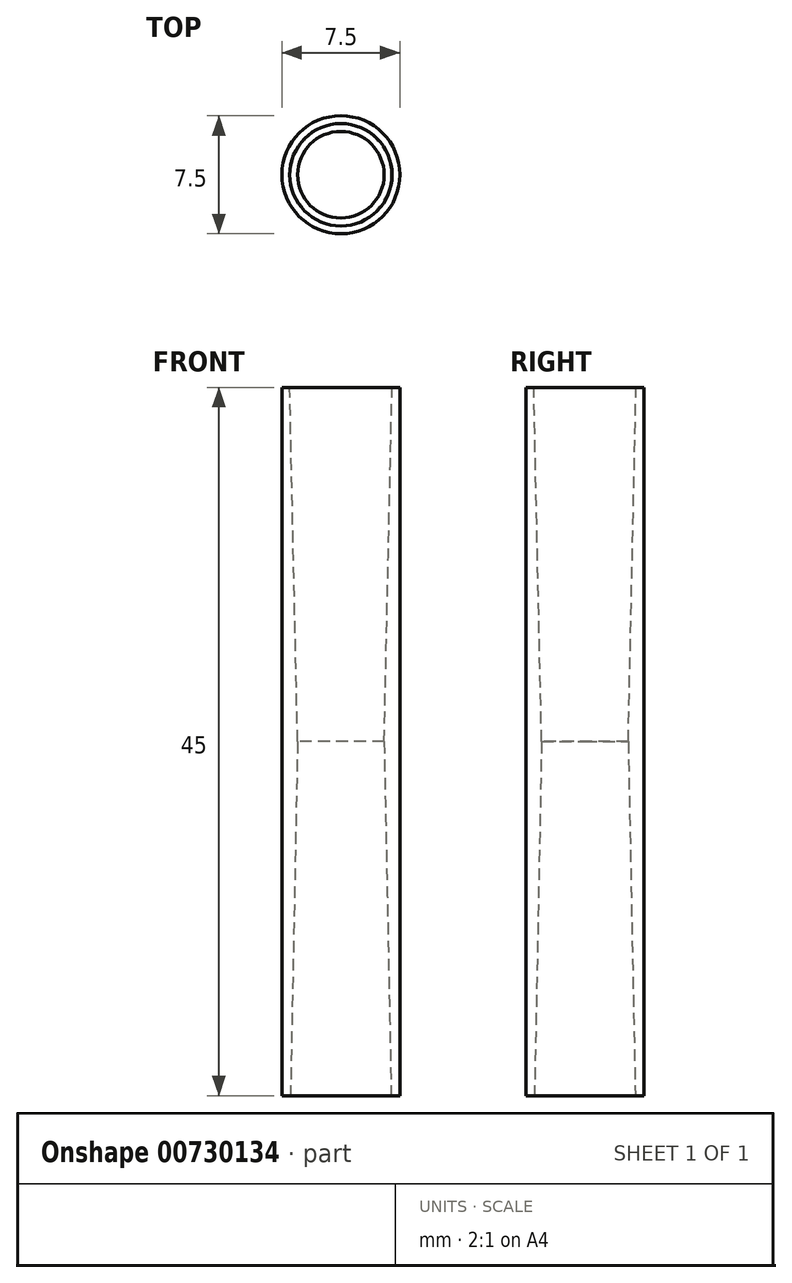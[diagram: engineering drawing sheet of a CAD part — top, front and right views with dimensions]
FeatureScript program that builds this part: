
annotation { "Feature Type Name" : "Feature", "Feature Type Description" : "" }
export const myFeature = defineFeature(function(context is Context, id is Id, definition is map)
    precondition{}
    {
        {
            var Q0;
            Q0=qCreatedBy(makeId("Top.planeOp"),FACE);
            var sketch = newSketch(context, id + "F0", { "sketchPlane" : qUnion([Q0])});
            skCircle(sketch, "E0", {"center": v(0, 0) * mm, "radius": 3.75 * mm});
            skSolve(sketch);
        }
        {
            var Q0;
            Q0=makeQuery(id+"F0.imprint","IMPRINT",FACE,{"disambiguationData":[TD([[makeQuery(id+"F0.imprint","IMPRINT",EDGE,{"derivedFrom":sQuery(id+"F0.wireOp",EDGE,"E0")}),1.0]])]});
            extrude(context, id + "F1", {"entities" : qUnion([Q0]), "depth" : 45 * mm, "offsetDistance" : 25 * mm});
        }
        {
            var Q0;
            Q0=makeQuery(id+"F0.imprint","IMPRINT",FACE,{"disambiguationData":[TD([[makeQuery(id+"F0.imprint","IMPRINT",EDGE,{"derivedFrom":sQuery(id+"F0.wireOp",EDGE,"E0")}),1.0]])]});
            var sketch = newSketch(context, id + "F2", { "sketchPlane" : qUnion([Q0])});
            skCircle(sketch, "E1", {"center": v(0, 0) * mm, "radius": 3.25 * mm});
            skSolve(sketch);
        }
        {
            var Q0;
            Q0=makeQuery(id+"F2.imprint","IMPRINT",FACE,{"disambiguationData":[TD([[makeQuery(id+"F2.imprint","IMPRINT",EDGE,{"derivedFrom":sQuery(id+"F2.wireOp",EDGE,"E1")}),1.0]])]});
            extrude(context, id + "F3", {"entities" : qUnion([Q0]), "operationType" : NewBodyOperationType.REMOVE, "oppositeDirection" : true, "depth" : (-(45 / 2)) * mm, "offsetDistance" : 25 * mm});
        }
        {
            var Q0;
            Q0=makeQuery(id+"F3.boolean.opBoolean","COPY",EDGE,{"derivedFrom":makeQuery(id+"F3.opExtrude","CAP_EDGE",EDGE,{"disambiguationData":[OSD([sQuery(id+"F2.wireOp",EDGE,"E1")])],"isStart":false})});
            chamfer(context, id + "F4", {"entities" : qUnion([Q0]), "chamferType" : ChamferType.TWO_OFFSETS, "width1" : 25 * mm, "oppositeDirection" : false, "width2" : 0.5 * mm, "tangentPropagation" : true});
        }
        {
            var Q0;
            Q0=makeQuery(id+"F1.opExtrude","CAP_FACE",FACE,{"disambiguationData":[OSD([sQuery(id+"F0.wireOp",EDGE,"E0")])],"isStart":false});
            var sketch = newSketch(context, id + "F5", { "sketchPlane" : qUnion([Q0])});
            skCircle(sketch, "E2", {"center": v(0, 0) * mm, "radius": 3.25 * mm});
            skSolve(sketch);
        }
        {
            var Q0;
            Q0=makeQuery(id+"F5.imprint","IMPRINT",FACE,{"disambiguationData":[TD([[makeQuery(id+"F5.imprint","IMPRINT",EDGE,{"derivedFrom":sQuery(id+"F5.wireOp",EDGE,"E2")}),1.0]])]});
            extrude(context, id + "F6", {"entities" : qUnion([Q0]), "operationType" : NewBodyOperationType.REMOVE, "oppositeDirection" : true, "depth" : (45 / 2) * mm, "offsetDistance" : 25 * mm});
        }
        {
            var Q0;
            Q0=makeQuery(id+"F6.boolean.opBoolean","COPY",EDGE,{"derivedFrom":makeQuery(id+"F6.opExtrude","CAP_EDGE",EDGE,{"disambiguationData":[OSD([sQuery(id+"F5.wireOp",EDGE,"E2")])],"isStart":false})});
            chamfer(context, id + "F7", {"entities" : qUnion([Q0]), "chamferType" : ChamferType.TWO_OFFSETS, "width1" : 0.5 * mm, "oppositeDirection" : false, "width2" : (45 / 2) * mm, "tangentPropagation" : true});
        }
    });
